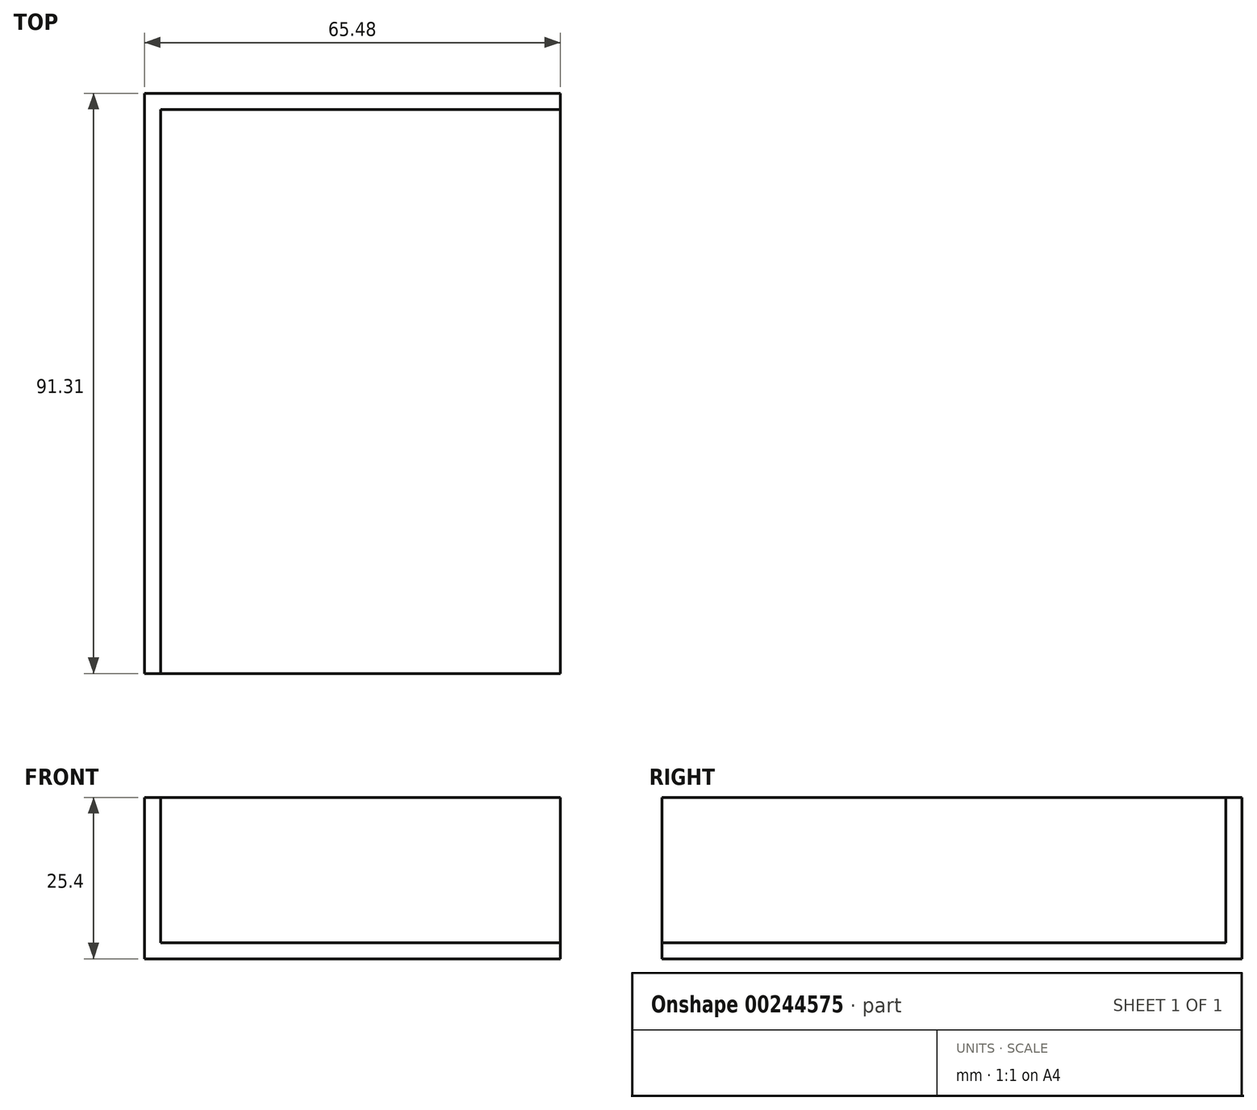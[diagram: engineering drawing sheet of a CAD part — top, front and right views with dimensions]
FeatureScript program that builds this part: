
annotation { "Feature Type Name" : "Feature", "Feature Type Description" : "" }
export const myFeature = defineFeature(function(context is Context, id is Id, definition is map)
    precondition{}
    {
        {
            var Q0;
            Q0=qCreatedBy(makeId("Top.planeOp"),FACE);
            var sketch = newSketch(context, id + "F2", { "sketchPlane" : qUnion([Q0])});
            skLineSegment(sketch, "E0.bottom", {"start": v(49.73, 77.82) * mm, "end": v(-15.75, 77.82) * mm});
            skLineSegment(sketch, "E0.top", {"start": v(49.73, -13.5) * mm, "end": v(-15.75, -13.5) * mm});
            skLineSegment(sketch, "E0.left", {"start": v(49.73, 77.82) * mm, "end": v(49.73, -13.5) * mm});
            skLineSegment(sketch, "E0.right", {"start": v(-15.75, 77.82) * mm, "end": v(-15.75, -13.5) * mm});
            skPoint(sketch, "E0.middle", {"position": v(17, 32.16) * mm});
            skSolve(sketch);
        }
        {
            var Q0;
            Q0 = qSketchRegion(id + "F2", true);
            extrude(context, id + "F0", {"entities" : qUnion([Q0]), "depth" : 25.4 * mm});
        }
        {
            var Q0;
            Q0=makeQuery(id+"F0.opExtrude","SWEPT_FACE",FACE,{"disambiguationData":[OSD([sQuery(id+"F2.wireOp",EDGE,"E0.left")])]});
            var Q1;
            Q1=makeQuery(id+"F0.opExtrude","SWEPT_FACE",FACE,{"disambiguationData":[OSD([sQuery(id+"F2.wireOp",EDGE,"E0.top")])]});
            var Q2;
            Q2=makeQuery(id+"F0.opExtrude","CAP_FACE",FACE,{"disambiguationData":[OSD([sQuery(id+"F2.wireOp",EDGE,"E0.bottom"),sQuery(id+"F2.wireOp",EDGE,"E0.top"),sQuery(id+"F2.wireOp",EDGE,"E0.left"),sQuery(id+"F2.wireOp",EDGE,"E0.right")])],"isStart":false});
            var Q3;
            Q3=makeQuery(id+"F0.opExtrude","SWEPT_BODY",BODY,{"disambiguationData":[OSD([sQuery(id+"F2.wireOp",EDGE,"E0.bottom"),sQuery(id+"F2.wireOp",EDGE,"E0.top"),sQuery(id+"F2.wireOp",EDGE,"E0.left"),sQuery(id+"F2.wireOp",EDGE,"E0.right")])]});
            shell(context, id + "F1", {"entities" : qUnion([Q0, Q1, Q2]), "parts" : qUnion([Q3]), "thickness" : 2.54 * mm});
        }
    });
